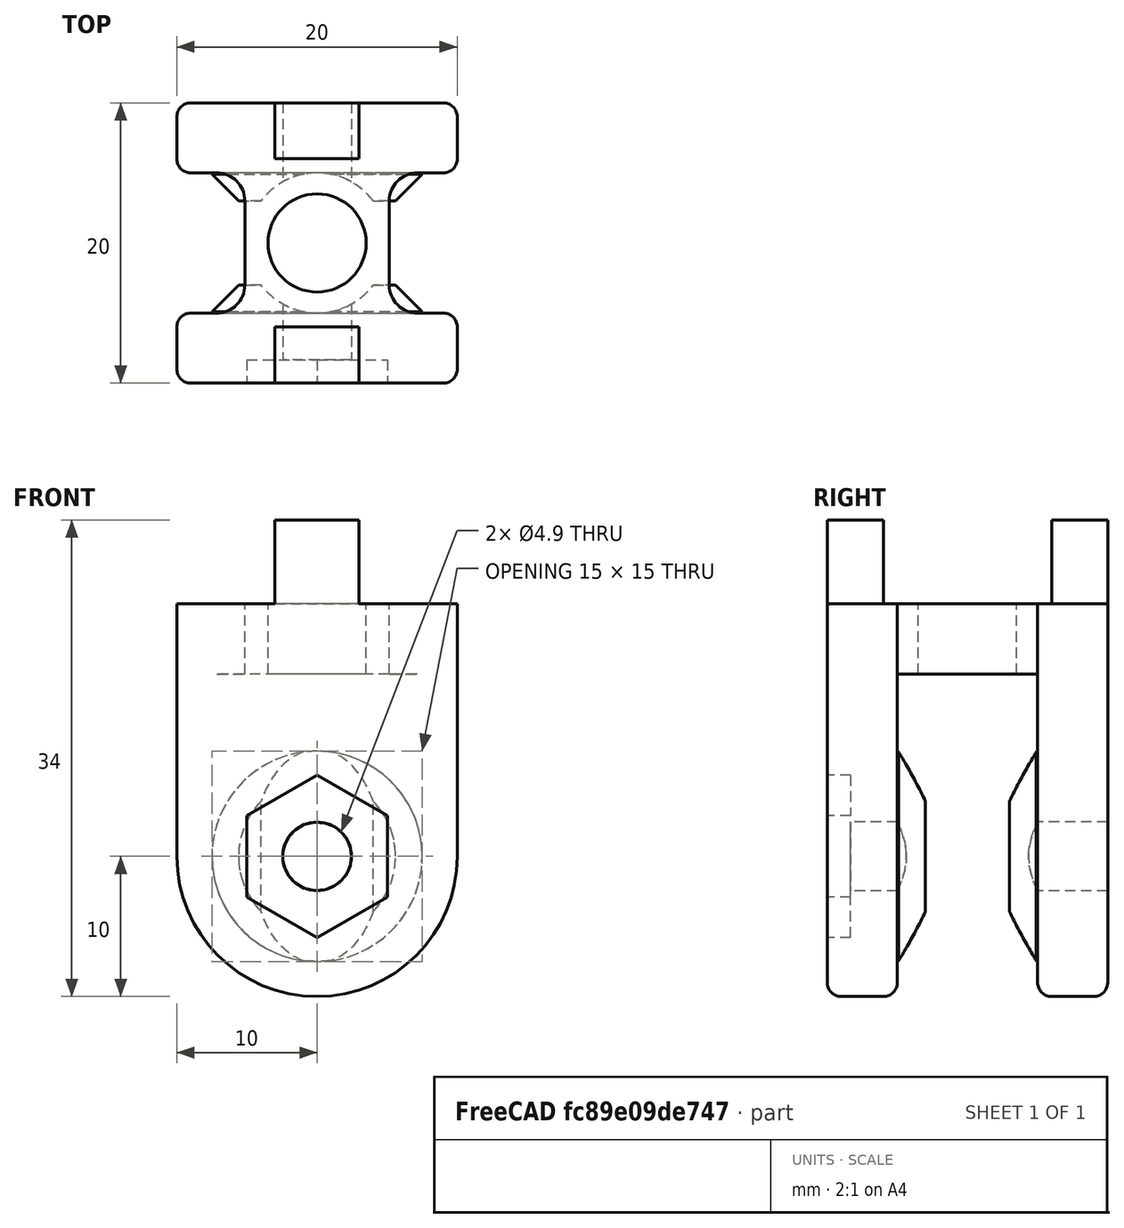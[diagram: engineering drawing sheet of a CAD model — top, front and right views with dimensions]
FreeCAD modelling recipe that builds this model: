
FCSTD DOCUMENT  (FreeCAD 0.19R24267 +99 (Git))
Label: ApoyoPoleaSimple
License: All rights reserved
LicenseURL: http://en.wikipedia.org/wiki/All_rights_reserved
objects: Part::Box×9, Part::Fillet×8, Part::Cylinder×7, Part::MultiFuse×4, Part::Fuse×4, Part::Chamfer×4, Part::Cut×3, Part::Prism×1, Part::Refine×1
note: 41 computed .brp shape members not serialized (recipe doc carries the construction recipe); baked Part::Feature solids carry a one-line shape summary decoded from their .brp

FEATURE [Part::Box] cube
  AttacherType = Attacher::AttachEngine3D
  Height = 5
  Length = 20
  Placement = pos=(-10,-10,0) rot=(0,0,1;0rad)
  Width = 20
FEATURE [Part::Cylinder] cylinder
  Angle = 360
  AttacherType = Attacher::AttachEngine3D
  Height = 100
  Placement = pos=(0,0,-50) rot=(0,0,1;0rad)
  Radius = 3.5
FEATURE [Part::Cut] difference
  Base = -> cube
  Tool = -> cylinder
FEATURE [Part::Box] cube001
  AttacherType = Attacher::AttachEngine3D
  Height = 11
  Length = 4
  Placement = pos=(6,-3,0) rot=(0,0,1;0rad)
  Width = 6
FEATURE [Part::Box] cube002
  AttacherType = Attacher::AttachEngine3D
  Height = 11
  Length = 4
  Placement = pos=(3,6,0) rot=(0,0,1;1.5708rad)
  Width = 6
FEATURE [Part::Box] cube003
  AttacherType = Attacher::AttachEngine3D
  Height = 11
  Length = 4
  Placement = pos=(-6,3,0) rot=(0,0,1;3.14159rad)
  Width = 6
FEATURE [Part::Box] cube004
  AttacherType = Attacher::AttachEngine3D
  Height = 11
  Length = 4
  Placement = pos=(-3,-6,0) rot=(0,0,-1;1.5708rad)
  Width = 6
FEATURE [Part::MultiFuse] Group
  Shapes = -> [cube001,cube002,cube003,cube004]
FEATURE [Part::Fuse] Group001
  Base = -> difference
  Tool = -> Group
FEATURE [Part::Box] cube005
  AttacherType = Attacher::AttachEngine3D
  Height = 100
  Length = 100
  Placement = pos=(5.15,-5,-50) rot=(0,0,1;0rad)
  Width = 10
FEATURE [Part::Box] cube006
  AttacherType = Attacher::AttachEngine3D
  Height = 100
  Length = 100
  Placement = pos=(-5.15,5,-50) rot=(0,0,1;3.14159rad)
  Width = 10
FEATURE [Part::Fuse] Group002
  Base = -> cube005
  Tool = -> cube006
FEATURE [Part::Cut] difference001
  Base = -> Group001
  Tool = -> Group002
FEATURE [Part::Box] cube007
  AttacherType = Attacher::AttachEngine3D
  Height = 13
  Length = 20
  Placement = pos=(-10,-10,-13) rot=(0,0,1;0rad)
  Width = 5
FEATURE [Part::Cylinder] cylinder001
  Angle = 360
  AttacherType = Attacher::AttachEngine3D
  Height = 5
  Placement = pos=(0,10,-13) rot=(1,0,0;1.5708rad)
  Radius = 10
FEATURE [Part::Cylinder] cylinder002
  Angle = 360
  AttacherType = Attacher::AttachEngine3D
  Height = 7
  Placement = pos=(0,10,-13) rot=(1,0,0;1.5708rad)
  Radius = 7.5
FEATURE [Part::MultiFuse] union
  Shapes = -> [cube007,cylinder001,cylinder002]
FEATURE [Part::Box] cube008
  AttacherType = Attacher::AttachEngine3D
  Height = 13
  Length = 20
  Placement = pos=(-10,-10,-13) rot=(0,0,1;0rad)
  Width = 5
FEATURE [Part::Cylinder] cylinder003
  Angle = 360
  AttacherType = Attacher::AttachEngine3D
  Height = 5
  Placement = pos=(0,10,-13) rot=(1,0,0;1.5708rad)
  Radius = 10
FEATURE [Part::Cylinder] cylinder004
  Angle = 360
  AttacherType = Attacher::AttachEngine3D
  Height = 7
  Placement = pos=(0,10,-13) rot=(1,0,0;1.5708rad)
  Radius = 7.5
FEATURE [Part::MultiFuse] union001
  Placement = pos=(0,0,0) rot=(0,0,1;3.14159rad)
  Shapes = -> [cube008,cylinder003,cylinder004]
FEATURE [Part::Fuse] Group003
  Base = -> union
  Tool = -> union001
FEATURE [Part::Cylinder] cylinder005
  Angle = 360
  AttacherType = Attacher::AttachEngine3D
  Height = 1000
  Placement = pos=(0,0,-500) rot=(0,0,1;0rad)
  Radius = 5
FEATURE [Part::Cylinder] cylinder006
  Angle = 360
  AttacherType = Attacher::AttachEngine3D
  Height = 1000
  Placement = pos=(0,500,-13) rot=(1,0,0;1.5708rad)
  Radius = 2.45
FEATURE [Part::Prism] prism
  AttacherType = Attacher::AttachEngine3D
  Circumradius = 5.79
  FirstAngle = 0
  Height = 5
  Placement = pos=(0,-8.33333,-13) rot=(0.57735,0.57735,-0.57735;2.0944rad)
  Polygon = 6
  SecondAngle = 0
FEATURE [Part::MultiFuse] union002
  Shapes = -> [cylinder005,cylinder006,prism]
FEATURE [Part::Cut] difference002
  Base = -> Group003
  Tool = -> union002
FEATURE [Part::Fuse] Group004
  Base = -> difference001
  Tool = -> difference002
FEATURE [Part::Refine] Group004001
  Source = -> Group004
FEATURE [Part::Chamfer] Chamfer
  Base = -> Group004001
  Edges = 1 edges r=1.9: [Edge115]
FEATURE [Part::Chamfer] Chamfer001
  Base = -> Chamfer
  Edges = 1 edges r=1.9: [Edge103]
FEATURE [Part::Chamfer] Chamfer002
  Base = -> Chamfer001
  Edges = 1 edges r=1.9: [Edge25]
FEATURE [Part::Chamfer] Chamfer003
  Base = -> Chamfer002
  Edges = 1 edges r=1.9: [Edge115]
FEATURE [Part::Fillet] Fillet
  Base = -> Chamfer003
  Edges = 1 edges r=2: [Edge23]
FEATURE [Part::Fillet] Fillet001
  Base = -> Fillet
  Edges = 1 edges r=2: [Edge54]
FEATURE [Part::Fillet] Fillet002
  Base = -> Fillet001
  Edges = 1 edges r=2: [Edge46]
FEATURE [Part::Fillet] Fillet003
  Base = -> Fillet002
  Edges = 1 edges r=2: [Edge25]
FEATURE [Part::Fillet] Fillet004
  Base = -> Fillet003
  Edges = 1 edges r=1: [Edge76]
FEATURE [Part::Fillet] Fillet005
  Base = -> Fillet004
  Edges = 1 edges r=1: [Edge79]
FEATURE [Part::Fillet] Fillet006
  Base = -> Fillet005
  Edges = 1 edges r=1: [Edge30]
FEATURE [Part::Fillet] Fillet007
  Base = -> Fillet006
  Edges = 1 edges r=1: [Edge77]
